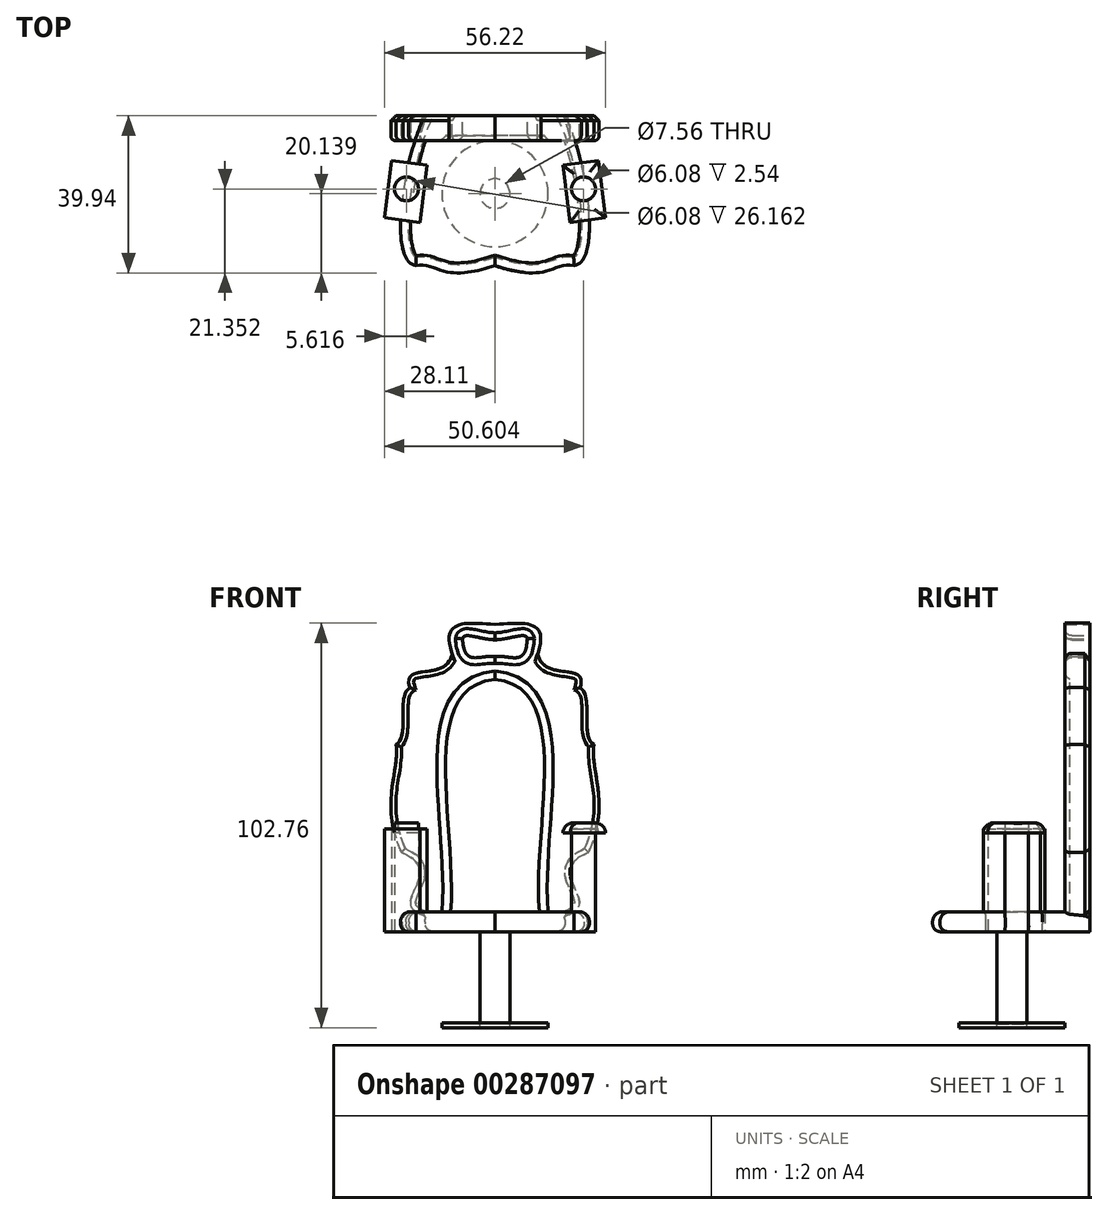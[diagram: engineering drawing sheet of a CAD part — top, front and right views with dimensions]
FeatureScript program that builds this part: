
annotation { "Feature Type Name" : "Feature", "Feature Type Description" : "" }
export const myFeature = defineFeature(function(context is Context, id is Id, definition is map)
    precondition{}
    {
        {
            var Q0;
            Q0=qCreatedBy(makeId("Front.planeOp"),FACE);
            var sketch = newSketch(context, id + "F0", { "sketchPlane" : qUnion([Q0])});
            skFitSpline(sketch, "E0", {"points": [v(0, 0) * mm, v(-17.85, 4.03) * mm], "startDerivative": vector(-17.32, 0) * mm, "endDerivative": vector(-6.38, 12.08) * mm});
            skFitSpline(sketch, "E1", {"points": [v(-17.85, 4.03) * mm, v(-23.76, 20.14) * mm], "startDerivative": vector(-31.41, 9.67) * mm, "endDerivative": vector(-37.05, 15.3) * mm});
            skFitSpline(sketch, "E2", {"points": [v(-23.76, 20.14) * mm, v(-25.1, 47.52) * mm], "startDerivative": vector(-16.91, 38.66) * mm, "endDerivative": vector(-2.42, 23.36) * mm});
            skFitSpline(sketch, "E3", {"points": [v(-25.1, 47.52) * mm, v(-21.61, 62.02) * mm], "startDerivative": vector(10.74, 6.71) * mm, "endDerivative": vector(10.74, 6.71) * mm});
            skLineSegment(sketch, "E4", {"start": v(0, -40.81) * mm, "end": v(0, 92.6) * mm, "construction": true});
            skFitSpline(sketch, "E5.MirrorCS", {"points": [v(25.1, 47.52) * mm, v(21.61, 62.02) * mm], "startDerivative": vector(-10.74, 6.71) * mm, "endDerivative": vector(-10.74, 6.71) * mm});
            skFitSpline(sketch, "E6.MirrorCS", {"points": [v(23.76, 20.14) * mm, v(25.1, 47.52) * mm], "startDerivative": vector(16.91, 38.66) * mm, "endDerivative": vector(2.42, 23.36) * mm});
            skFitSpline(sketch, "E7.MirrorCS", {"points": [v(17.85, 4.03) * mm, v(23.76, 20.14) * mm], "startDerivative": vector(31.41, 9.67) * mm, "endDerivative": vector(37.05, 15.3) * mm});
            skFitSpline(sketch, "E8.MirrorCS", {"points": [v(0, 0) * mm, v(17.85, 4.03) * mm], "startDerivative": vector(17.32, 0) * mm, "endDerivative": vector(6.38, 12.08) * mm});
            skFitSpline(sketch, "E9", {"points": [v(-21.61, 62.02) * mm, v(-10.85, 70.64) * mm], "startDerivative": vector(-6.97, 20.51) * mm, "endDerivative": vector(4.46, 22.3) * mm});
            skFitSpline(sketch, "E10", {"points": [v(-10.85, 70.64) * mm, v(0, 78.08) * mm], "startDerivative": vector(-8.92, 25.87) * mm, "endDerivative": vector(23.64, -1.78) * mm});
            skFitSpline(sketch, "E11.MirrorCS", {"points": [v(10.85, 70.64) * mm, v(0, 78.08) * mm], "startDerivative": vector(8.92, 25.87) * mm, "endDerivative": vector(-23.64, -1.78) * mm});
            skFitSpline(sketch, "E12.MirrorCS", {"points": [v(21.61, 62.02) * mm, v(10.85, 70.64) * mm], "startDerivative": vector(6.97, 20.51) * mm, "endDerivative": vector(-4.46, 22.3) * mm});
            skFitSpline(sketch, "E13", {"points": [v(-11.8, 0.76) * mm, v(0, 64.1) * mm], "startDerivative": vector(11.8, 63.33) * mm, "endDerivative": vector(64.84, 6.24) * mm});
            skFitSpline(sketch, "E14.MirrorCS", {"points": [v(11.8, 0.76) * mm, v(0, 64.1) * mm], "startDerivative": vector(-11.8, 63.33) * mm, "endDerivative": vector(-64.84, 6.24) * mm});
            skFitSpline(sketch, "E15", {"points": [v(0, 74.16) * mm, v(-8.22, 74.4) * mm], "startDerivative": vector(-13.43, 0.62) * mm, "endDerivative": vector(-1.16, -5.63) * mm});
            skFitSpline(sketch, "E16", {"points": [v(-8.22, 74.4) * mm, v(0, 69.9) * mm], "startDerivative": vector(1.23, -21.89) * mm, "endDerivative": vector(12.5, -1.6) * mm});
            skFitSpline(sketch, "E17.MirrorCS", {"points": [v(8.22, 74.4) * mm, v(0, 69.9) * mm], "startDerivative": vector(-1.23, -21.89) * mm, "endDerivative": vector(-12.5, -1.6) * mm});
            skFitSpline(sketch, "E18.MirrorCS", {"points": [v(0, 74.16) * mm, v(8.22, 74.4) * mm], "startDerivative": vector(13.43, 0.62) * mm, "endDerivative": vector(1.16, -5.63) * mm});
            skSolve(sketch);
        }
        {
            var Q0;
            Q0=qCreatedBy(makeId("Top.planeOp"),FACE);
            var sketch = newSketch(context, id + "F1", { "sketchPlane" : qUnion([Q0])});
            skFitSpline(sketch, "E19", {"points": [v(-17.78, 0) * mm, v(-20.02, -38.1) * mm], "startDerivative": vector(-16.5, -32.16) * mm, "endDerivative": vector(22.01, -2.37) * mm});
            skFitSpline(sketch, "E20", {"points": [v(-20.02, -38.1) * mm, v(0, -38.1) * mm], "startDerivative": vector(17.3, 3.17) * mm, "endDerivative": vector(42.75, 13.87) * mm});
            skLineSegment(sketch, "E21", {"start": v(0, -45.95) * mm, "end": v(0, 45.3) * mm, "construction": true});
            skFitSpline(sketch, "E22.MirrorCS", {"points": [v(17.78, 0) * mm, v(20.02, -38.1) * mm], "startDerivative": vector(16.5, -32.16) * mm, "endDerivative": vector(-22.01, -2.37) * mm});
            skFitSpline(sketch, "E23.MirrorCS", {"points": [v(20.02, -38.1) * mm, v(0, -38.1) * mm], "startDerivative": vector(-17.3, 3.17) * mm, "endDerivative": vector(-42.75, 13.87) * mm});
            skLineSegment(sketch, "E24", {"start": v(-17.78, 0) * mm, "end": v(17.78, 0) * mm});
            skLineSegment(sketch, "E25", {"start": v(-6.58, 0) * mm, "end": v(-6.58, 4.83) * mm});
            skLineSegment(sketch, "E26", {"start": v(-6.58, 4.83) * mm, "end": v(0, 4.83) * mm});
            skLineSegment(sketch, "E27.MirrorCS", {"start": v(6.58, 4.83) * mm, "end": v(0, 4.83) * mm});
            skLineSegment(sketch, "E28.MirrorCS", {"start": v(6.58, 0) * mm, "end": v(6.58, 4.83) * mm});
            skSolve(sketch);
        }
        {
            var Q0;
            {var subQ3=sQuery(id+"F0.wireOp",EDGE,"E1");Q0=makeQuery(id+"F0.imprint","IMPRINT",FACE,{"disambiguationData":[TD([[makeQuery(id+"F0.imprint","IMPRINT",EDGE,{"derivedFrom":subQ3}),-1.0]])]});}
            extrude(context, id + "F2", {"entities" : qUnion([Q0]), "depth" : 6.35 * mm});
        }
        {
            var Q0;
            {var subQ3=sQuery(id+"F0.wireOp",EDGE,"E13");Q0=makeQuery(id+"F0.imprint","IMPRINT",FACE,{"disambiguationData":[TD([[makeQuery(id+"F0.imprint","IMPRINT",EDGE,{"derivedFrom":subQ3}),-1.0]])]});}
            extrude(context, id + "F3", {"entities" : qUnion([Q0]), "operationType" : NewBodyOperationType.ADD, "depth" : 5.08 * mm});
        }
        {
            var Q0;
            {var subQ1=sQuery(id+"F1.wireOp",EDGE,"E19");Q0=makeQuery(id+"F1.imprint","IMPRINT",FACE,{"disambiguationData":[TD([[makeQuery(id+"F1.imprint","IMPRINT",EDGE,{"derivedFrom":subQ1}),1.0]])]});}
            extrude(context, id + "F4", {"entities" : qUnion([Q0]), "operationType" : NewBodyOperationType.ADD, "depth" : 5.08 * mm});
        }
        {
            var Q0;
            Q0=makeQuery(id+"F4.opExtrude","CAP_EDGE",EDGE,{"disambiguationData":[OSD([sQuery(id+"F1.wireOp",EDGE,"E23.MirrorCS")])],"isStart":false});
            var Q1;
            Q1=makeQuery(id+"F4.opExtrude","CAP_EDGE",EDGE,{"disambiguationData":[OSD([sQuery(id+"F1.wireOp",EDGE,"E20")])],"isStart":false});
            var Q2;
            Q2=makeQuery(id+"F4.opExtrude","CAP_EDGE",EDGE,{"disambiguationData":[OSD([sQuery(id+"F1.wireOp",EDGE,"E22.MirrorCS")])],"isStart":false});
            var Q3;
            Q3=makeQuery(id+"F4.opExtrude","CAP_EDGE",EDGE,{"disambiguationData":[OSD([sQuery(id+"F1.wireOp",EDGE,"E19")])],"isStart":false});
            fillet(context, id + "F5", {"entities" : qUnion([Q0, Q1, Q2, Q3]), "radius" : 2.54 * mm, "tangentPropagation" : true, "allowEdgeOverflow" : false});
        }
        {
            var Q0;
            Q0=makeQuery(id+"F4.opExtrude","CAP_EDGE",EDGE,{"disambiguationData":[OSD([sQuery(id+"F1.wireOp",EDGE,"E19")])],"isStart":true});
            var Q1;
            Q1=makeQuery(id+"F4.opExtrude","CAP_EDGE",EDGE,{"disambiguationData":[OSD([sQuery(id+"F1.wireOp",EDGE,"E20")])],"isStart":true});
            var Q2;
            Q2=makeQuery(id+"F4.opExtrude","CAP_EDGE",EDGE,{"disambiguationData":[OSD([sQuery(id+"F1.wireOp",EDGE,"E23.MirrorCS")])],"isStart":true});
            var Q3;
            Q3=makeQuery(id+"F4.opExtrude","CAP_EDGE",EDGE,{"disambiguationData":[OSD([sQuery(id+"F1.wireOp",EDGE,"E22.MirrorCS")])],"isStart":true});
            fillet(context, id + "F6", {"entities" : qUnion([Q0, Q1, Q2, Q3]), "radius" : 2.03 * mm, "tangentPropagation" : true, "allowEdgeOverflow" : false});
        }
        {
            var Q0;
            Q0=makeQuery(id+"F2.opExtrude","CAP_EDGE",EDGE,{"disambiguationData":[OSD([sQuery(id+"F0.wireOp",EDGE,"E13")])],"isStart":false});
            var Q1;
            Q1=makeQuery(id+"F2.opExtrude","CAP_EDGE",EDGE,{"disambiguationData":[OSD([sQuery(id+"F0.wireOp",EDGE,"E14.MirrorCS")])],"isStart":false});
            fillet(context, id + "F7", {"entities" : qUnion([Q0, Q1]), "radius" : 2.54 * mm, "tangentPropagation" : true, "allowEdgeOverflow" : false});
        }
        {
            var Q0;
            Q0=makeQuery(id+"F2.opExtrude","CAP_EDGE",EDGE,{"disambiguationData":[OSD([sQuery(id+"F0.wireOp",EDGE,"E9")])],"isStart":false});
            var Q1;
            Q1=makeQuery(id+"F2.opExtrude","CAP_EDGE",EDGE,{"disambiguationData":[OSD([sQuery(id+"F0.wireOp",EDGE,"E3")])],"isStart":false});
            var Q2;
            Q2=makeQuery(id+"F2.opExtrude","CAP_EDGE",EDGE,{"disambiguationData":[OSD([sQuery(id+"F0.wireOp",EDGE,"E2")])],"isStart":false});
            var Q3;
            Q3=makeQuery(id+"F2.opExtrude","CAP_EDGE",EDGE,{"disambiguationData":[OSD([sQuery(id+"F0.wireOp",EDGE,"E1")])],"isStart":false});
            var Q4;
            Q4=makeQuery(id+"F2.opExtrude","CAP_EDGE",EDGE,{"disambiguationData":[OSD([sQuery(id+"F0.wireOp",EDGE,"E7.MirrorCS")])],"isStart":false});
            var Q5;
            Q5=makeQuery(id+"F2.opExtrude","CAP_EDGE",EDGE,{"disambiguationData":[OSD([sQuery(id+"F0.wireOp",EDGE,"E6.MirrorCS")])],"isStart":false});
            var Q6;
            Q6=makeQuery(id+"F2.opExtrude","CAP_EDGE",EDGE,{"disambiguationData":[OSD([sQuery(id+"F0.wireOp",EDGE,"E5.MirrorCS")])],"isStart":false});
            var Q7;
            Q7=makeQuery(id+"F2.opExtrude","CAP_EDGE",EDGE,{"disambiguationData":[OSD([sQuery(id+"F0.wireOp",EDGE,"E12.MirrorCS")])],"isStart":false});
            fillet(context, id + "F8", {"entities" : qUnion([Q0, Q1, Q2, Q3, Q4, Q5, Q6, Q7]), "radius" : 1.27 * mm, "tangentPropagation" : true, "allowEdgeOverflow" : false});
        }
        {
            var Q0;
            Q0=makeQuery(id+"F2.opExtrude","CAP_EDGE",EDGE,{"disambiguationData":[OSD([sQuery(id+"F0.wireOp",EDGE,"E18.MirrorCS")])],"isStart":false});
            var Q1;
            Q1=makeQuery(id+"F2.opExtrude","CAP_EDGE",EDGE,{"disambiguationData":[OSD([sQuery(id+"F0.wireOp",EDGE,"E15")])],"isStart":false});
            var Q2;
            Q2=makeQuery(id+"F2.opExtrude","CAP_EDGE",EDGE,{"disambiguationData":[OSD([sQuery(id+"F0.wireOp",EDGE,"E16")])],"isStart":false});
            var Q3;
            Q3=makeQuery(id+"F2.opExtrude","CAP_EDGE",EDGE,{"disambiguationData":[OSD([sQuery(id+"F0.wireOp",EDGE,"E17.MirrorCS")])],"isStart":false});
            fillet(context, id + "F9", {"entities" : qUnion([Q0, Q1, Q2, Q3]), "radius" : 1.78 * mm, "tangentPropagation" : true, "allowEdgeOverflow" : false});
        }
        {
            var Q0;
            Q0=makeQuery(id+"F2.opExtrude","CAP_EDGE",EDGE,{"disambiguationData":[OSD([sQuery(id+"F0.wireOp",EDGE,"E6.MirrorCS")])],"isStart":true});
            var Q1;
            Q1=makeQuery(id+"F2.opExtrude","CAP_EDGE",EDGE,{"disambiguationData":[OSD([sQuery(id+"F0.wireOp",EDGE,"E5.MirrorCS")])],"isStart":true});
            var Q2;
            Q2=makeQuery(id+"F2.opExtrude","CAP_EDGE",EDGE,{"disambiguationData":[OSD([sQuery(id+"F0.wireOp",EDGE,"E2")])],"isStart":true});
            var Q3;
            Q3=makeQuery(id+"F2.opExtrude","CAP_EDGE",EDGE,{"disambiguationData":[OSD([sQuery(id+"F0.wireOp",EDGE,"E3")])],"isStart":true});
            var Q4;
            Q4=makeQuery(id+"F2.opExtrude","CAP_EDGE",EDGE,{"disambiguationData":[OSD([sQuery(id+"F0.wireOp",EDGE,"E1")])],"isStart":true});
            var Q5;
            Q5=makeQuery(id+"F2.opExtrude","CAP_EDGE",EDGE,{"disambiguationData":[OSD([sQuery(id+"F0.wireOp",EDGE,"E7.MirrorCS")])],"isStart":true});
            var Q6;
            Q6=makeQuery(id+"F2.opExtrude","CAP_EDGE",EDGE,{"disambiguationData":[OSD([sQuery(id+"F0.wireOp",EDGE,"E9")])],"isStart":true});
            var Q7;
            Q7=makeQuery(id+"F2.opExtrude","CAP_EDGE",EDGE,{"disambiguationData":[OSD([sQuery(id+"F0.wireOp",EDGE,"E12.MirrorCS")])],"isStart":true});
            chamfer(context, id + "F10", {"entities" : qUnion([Q0, Q1, Q2, Q3, Q4, Q5, Q6, Q7]), "width" : 1.27 * mm, "tangentPropagation" : true});
        }
        {
            var Q0;
            Q0=qCreatedBy(makeId("Top.planeOp"),FACE);
            var sketch = newSketch(context, id + "F11", { "sketchPlane" : qUnion([Q0])});
            skLineSegment(sketch, "E29", {"start": v(0, -50.1) * mm, "end": v(0, 55.9) * mm, "construction": true});
            skCircle(sketch, "E30", {"center": v(22.5, -18.59) * mm, "radius": 3.04 * mm});
            skCircle(sketch, "E31.MirrorC", {"center": v(-22.5, -18.59) * mm, "radius": 3.04 * mm});
            skLineSegment(sketch, "E32", {"start": v(-19.09, -27.1) * mm, "end": v(-17.28, -12.57) * mm});
            skLineSegment(sketch, "E33", {"start": v(-17.28, -12.57) * mm, "end": v(-26.31, -11.45) * mm});
            skLineSegment(sketch, "E34", {"start": v(-26.31, -11.45) * mm, "end": v(-28.11, -25.94) * mm});
            skLineSegment(sketch, "E35", {"start": v(-28.11, -25.94) * mm, "end": v(-19.09, -27.1) * mm});
            skLineSegment(sketch, "E36.MirrorCS", {"start": v(19.09, -27.1) * mm, "end": v(17.28, -12.57) * mm});
            skLineSegment(sketch, "E37.MirrorCS", {"start": v(17.28, -12.57) * mm, "end": v(26.31, -11.45) * mm});
            skLineSegment(sketch, "E38.MirrorCS", {"start": v(26.31, -11.45) * mm, "end": v(28.11, -25.94) * mm});
            skLineSegment(sketch, "E39.MirrorCS", {"start": v(28.11, -25.94) * mm, "end": v(19.09, -27.1) * mm});
            skSolve(sketch);
        }
        {
            var Q0;
            Q0=makeQuery(id+"F11.imprint","IMPRINT",FACE,{"disambiguationData":[TD([[makeQuery(id+"F11.imprint","IMPRINT",EDGE,{"derivedFrom":sQuery(id+"F11.wireOp",EDGE,"E30")}),1.0]])]});
            var Q1;
            Q1=makeQuery(id+"F11.imprint","IMPRINT",FACE,{"disambiguationData":[TD([[makeQuery(id+"F11.imprint","IMPRINT",EDGE,{"derivedFrom":sQuery(id+"F11.wireOp",EDGE,"E31.MirrorC")}),-1.0]])]});
            extrude(context, id + "F12", {"entities" : qUnion([Q0, Q1]), "operationType" : NewBodyOperationType.ADD, "depth" : 26.16 * mm});
        }
        {
            var Q0;
            Q0=makeQuery(id+"F11.imprint","IMPRINT",FACE,{"disambiguationData":[TD([[makeQuery(id+"F11.imprint","IMPRINT",EDGE,{"derivedFrom":sQuery(id+"F11.wireOp",EDGE,"E31.MirrorC")}),1.0]])]});
            var Q1;
            Q1=makeQuery(id+"F11.imprint","IMPRINT",FACE,{"disambiguationData":[TD([[makeQuery(id+"F11.imprint","IMPRINT",EDGE,{"derivedFrom":sQuery(id+"F11.wireOp",EDGE,"E30")}),-1.0]])]});
            extrude(context, id + "F13", {"entities" : qUnion([Q0, Q1]), "depth" : 2.54 * mm});
        }
        {
            var Q0;
            Q0=qCreatedBy(makeId("Top.planeOp"),FACE);
            var sketch = newSketch(context, id + "F14", { "sketchPlane" : qUnion([Q0])});
            skCircle(sketch, "E40", {"center": v(0, -19.8) * mm, "radius": 3.78 * mm});
            skCircle(sketch, "E41", {"center": v(0, -19.8) * mm, "radius": 13.49 * mm});
            skSolve(sketch);
        }
        {
            var Q0;
            Q0=makeQuery(id+"F14.imprint","IMPRINT",FACE,{"disambiguationData":[TD([[makeQuery(id+"F14.imprint","IMPRINT",EDGE,{"derivedFrom":sQuery(id+"F14.wireOp",EDGE,"E40")}),1.0]])]});
            extrude(context, id + "F15", {"entities" : qUnion([Q0]), "operationType" : NewBodyOperationType.ADD, "oppositeDirection" : true, "depth" : 23.37 * mm});
        }
        {
            var Q0;
            Q0=makeQuery(id+"F14.imprint","IMPRINT",FACE,{"disambiguationData":[TD([[makeQuery(id+"F14.imprint","IMPRINT",EDGE,{"derivedFrom":sQuery(id+"F14.wireOp",EDGE,"E40")}),-1.0]])]});
            extrude(context, id + "F16", {"entities" : qUnion([Q0]), "oppositeDirection" : true, "depth" : 1.27 * mm});
        }
        {
            var Q0;
            Q0=makeQuery(id+"F16.opExtrude","SWEPT_BODY",BODY,{"disambiguationData":[OSD([sQuery(id+"F14.wireOp",EDGE,"E40"),sQuery(id+"F14.wireOp",EDGE,"E41")])]});
            transform(context, id + "F17", {"entities" : qUnion([Q0]), "transformType" : TransformType.TRANSLATION_3D, "dx" : 0 * mm, "dy" : 0 * mm, "dz" : -23.1 * mm, "makeCopy" : false});
        }
        {
            var Q0;
            Q0=makeQuery(id+"F13.opExtrude","SWEPT_BODY",BODY,{"disambiguationData":[OSD([sQuery(id+"F11.wireOp",EDGE,"E30"),sQuery(id+"F11.wireOp",EDGE,"E36.MirrorCS"),sQuery(id+"F11.wireOp",EDGE,"E37.MirrorCS"),sQuery(id+"F11.wireOp",EDGE,"E38.MirrorCS"),sQuery(id+"F11.wireOp",EDGE,"E39.MirrorCS")])]});
            var Q1;
            Q1=makeQuery(id+"F13.opExtrude","SWEPT_BODY",BODY,{"disambiguationData":[OSD([sQuery(id+"F11.wireOp",EDGE,"E31.MirrorC"),sQuery(id+"F11.wireOp",EDGE,"E32"),sQuery(id+"F11.wireOp",EDGE,"E33"),sQuery(id+"F11.wireOp",EDGE,"E34"),sQuery(id+"F11.wireOp",EDGE,"E35")])]});
            transform(context, id + "F18", {"entities" : qUnion([Q0, Q1]), "transformType" : TransformType.TRANSLATION_3D, "dx" : 0 * mm, "dy" : 0 * mm, "dz" : 25.15 * mm, "makeCopy" : false});
        }
        {
            var Q0;
            Q0=makeQuery(id+"F13.opExtrude","CAP_EDGE",EDGE,{"disambiguationData":[OSD([sQuery(id+"F11.wireOp",EDGE,"E39.MirrorCS")])],"isStart":false});
            var Q1;
            Q1=makeQuery(id+"F13.opExtrude","CAP_EDGE",EDGE,{"disambiguationData":[OSD([sQuery(id+"F11.wireOp",EDGE,"E35")])],"isStart":false});
            var Q2;
            Q2=makeQuery(id+"F13.opExtrude","CAP_EDGE",EDGE,{"disambiguationData":[OSD([sQuery(id+"F11.wireOp",EDGE,"E32")])],"isStart":false});
            var Q3;
            Q3=makeQuery(id+"F13.opExtrude","CAP_EDGE",EDGE,{"disambiguationData":[OSD([sQuery(id+"F11.wireOp",EDGE,"E36.MirrorCS")])],"isStart":false});
            var Q4;
            Q4=makeQuery(id+"F13.opExtrude","CAP_EDGE",EDGE,{"disambiguationData":[OSD([sQuery(id+"F11.wireOp",EDGE,"E38.MirrorCS")])],"isStart":false});
            var Q5;
            Q5=makeQuery(id+"F13.opExtrude","CAP_EDGE",EDGE,{"disambiguationData":[OSD([sQuery(id+"F11.wireOp",EDGE,"E34")])],"isStart":false});
            var Q6;
            Q6=makeQuery(id+"F13.opExtrude","CAP_EDGE",EDGE,{"disambiguationData":[OSD([sQuery(id+"F11.wireOp",EDGE,"E33")])],"isStart":false});
            var Q7;
            Q7=makeQuery(id+"F13.opExtrude","CAP_EDGE",EDGE,{"disambiguationData":[OSD([sQuery(id+"F11.wireOp",EDGE,"E37.MirrorCS")])],"isStart":false});
            fillet(context, id + "F19", {"entities" : qUnion([Q0, Q1, Q2, Q3, Q4, Q5, Q6, Q7]), "radius" : 2.54 * mm, "tangentPropagation" : true, "allowEdgeOverflow" : false});
        }
    });
